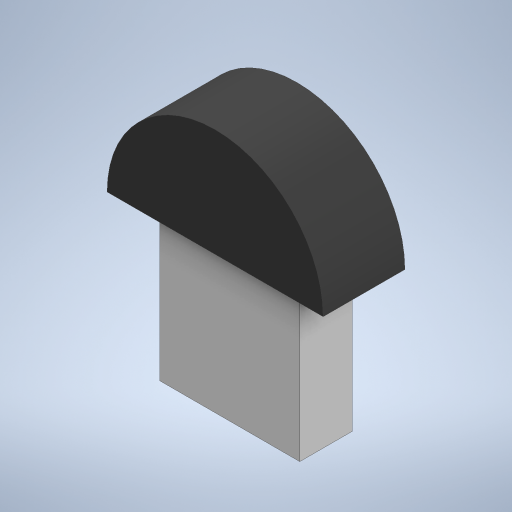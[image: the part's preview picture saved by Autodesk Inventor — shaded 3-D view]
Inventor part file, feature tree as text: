
AUTODESK INVENTOR PART (.ipt)
format: ipt  version: 2023.1 (Build 271208000, 208)  size: 230,400 bytes
history: native  units: mm
features: extrude x2, other x1, sketch x1
ambient origin geometry x8: Origin, YZ Plane, XZ Plane, XY Plane, X Axis, Y Axis, Z Axis, Center Point
bodies: Body1 (feature_tree)
feature tree (4):
  other  "솔리드1"
  sketch  "스케치1"
  extrude  "돌출1"  Depth=18.5mm
  extrude  "돌출2"  Depth=9.25mm
